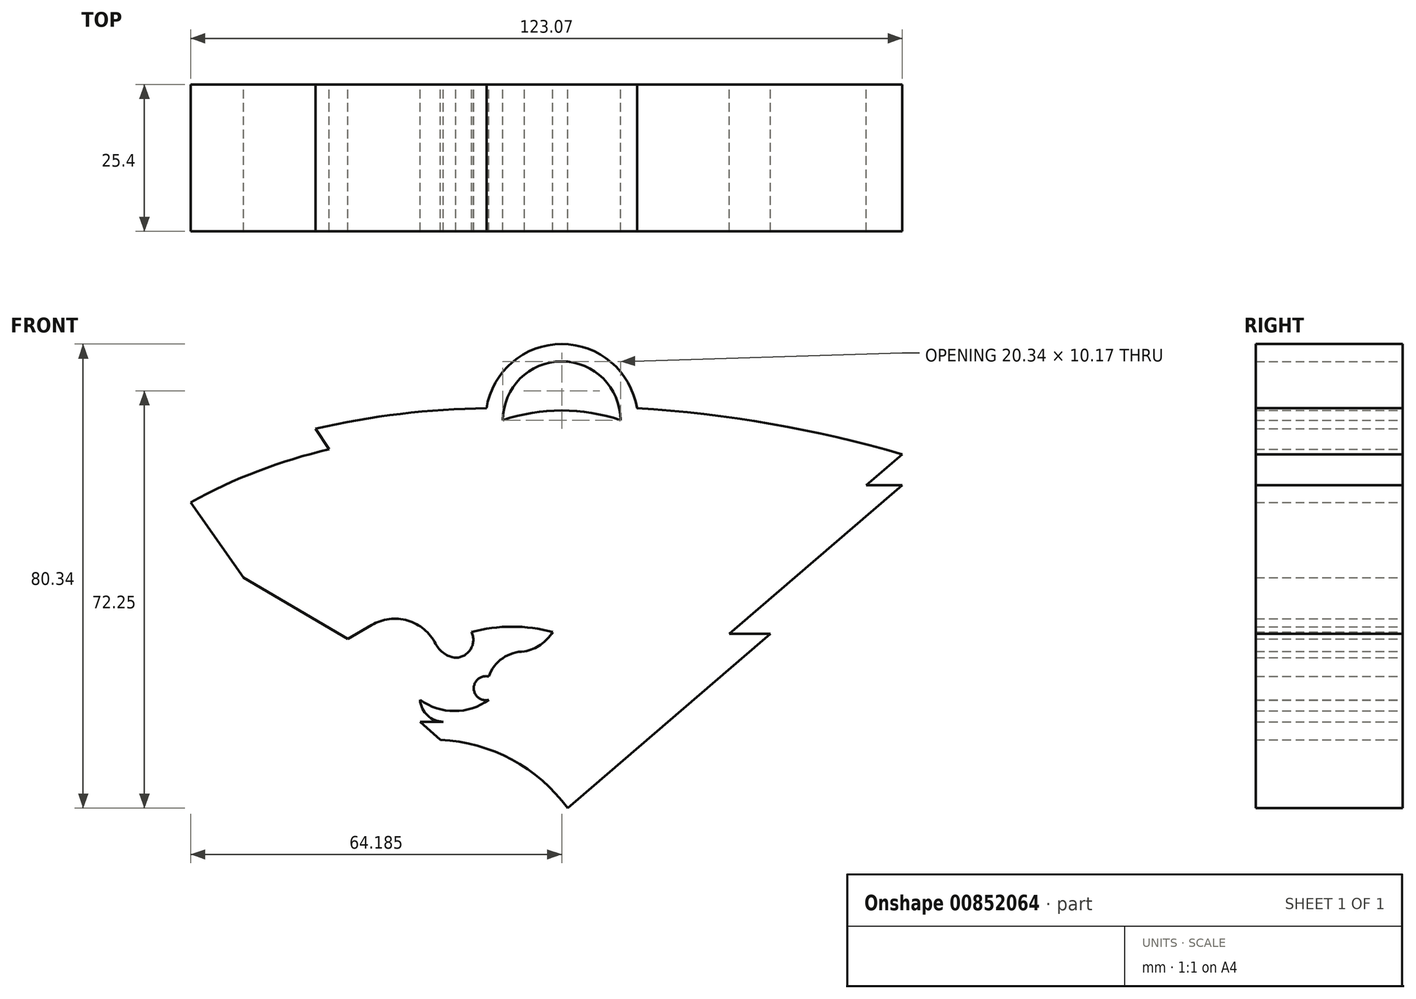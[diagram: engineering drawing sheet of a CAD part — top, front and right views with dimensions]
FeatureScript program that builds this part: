
annotation { "Feature Type Name" : "Feature", "Feature Type Description" : "" }
export const myFeature = defineFeature(function(context is Context, id is Id, definition is map)
    precondition{}
    {
        {
            var Q0;
            Q0=qCreatedBy(makeId("Front.planeOp"),FACE);
            var sketch = newSketch(context, id + "F0", { "sketchPlane" : qUnion([Q0])});
            skLineSegment(sketch, "E0", {"start": v(0, -55.9) * mm, "end": v(35.05, -25.73) * mm});
            skLineSegment(sketch, "E1", {"start": v(35.05, -25.73) * mm, "end": v(27.95, -25.73) * mm});
            skLineSegment(sketch, "E2", {"start": v(27.95, -25.73) * mm, "end": v(57.85, 0) * mm});
            skLineSegment(sketch, "E3", {"start": v(57.85, 0) * mm, "end": v(51.61, 0) * mm});
            skLineSegment(sketch, "E4", {"start": v(51.61, 0) * mm, "end": v(57.85, 5.37) * mm});
            skArc(sketch, "E5", {"start": v(57.85, 5.37) * mm, "mid": v(35.14, 10.63) * mm, "end": v(11.98, 13.31) * mm});
            skArc(sketch, "E6", {"start": v(11.98, 13.31) * mm, "mid": v(-1.04, 24.44) * mm, "end": v(-14.05, 13.31) * mm});
            skArc(sketch, "E7", {"start": v(-14.05, 13.31) * mm, "mid": v(-28.94, 12.34) * mm, "end": v(-43.63, 9.76) * mm});
            skLineSegment(sketch, "E8", {"start": v(-43.63, 9.76) * mm, "end": v(-41.26, 6.21) * mm});
            skArc(sketch, "E9", {"start": v(-41.26, 6.21) * mm, "mid": v(-53.56, 2.45) * mm, "end": v(-65.22, -2.96) * mm});
            skLineSegment(sketch, "E10", {"start": v(-65.22, -2.96) * mm, "end": v(-56.05, -15.97) * mm});
            skLineSegment(sketch, "E11", {"start": v(-56.05, -15.97) * mm, "end": v(-38, -26.62) * mm});
            skArc(sketch, "E12", {"start": v(0, -55.9) * mm, "mid": v(-9.67, -47.48) * mm, "end": v(-22.04, -44.07) * mm});
            skLineSegment(sketch, "E13", {"start": v(-38, -26.62) * mm, "end": v(-33.9, -24.2) * mm});
            skArc(sketch, "E14", {"start": v(-22.83, -27.44) * mm, "mid": v(-27.67, -23.43) * mm, "end": v(-33.9, -24.2) * mm});
            skArc(sketch, "E15", {"start": v(-22.83, -27.44) * mm, "mid": v(-21.39, -29.1) * mm, "end": v(-19.33, -29.87) * mm});
            skLineSegment(sketch, "E16", {"start": v(-22.04, -44.07) * mm, "end": v(-25.53, -40.93) * mm});
            skLineSegment(sketch, "E17", {"start": v(-25.53, -40.93) * mm, "end": v(-21.48, -40.93) * mm});
            skArc(sketch, "E18", {"start": v(-25.53, -37.15) * mm, "mid": v(-24.25, -39.84) * mm, "end": v(-21.48, -40.93) * mm});
            skArc(sketch, "E19", {"start": v(-25.53, -37.15) * mm, "mid": v(-19.6, -39.08) * mm, "end": v(-13.66, -37.15) * mm});
            skArc(sketch, "E20", {"start": v(-13.66, -33.1) * mm, "mid": v(-16.24, -35.13) * mm, "end": v(-13.66, -37.15) * mm});
            skArc(sketch, "E21", {"start": v(-7.46, -28.8) * mm, "mid": v(-11.26, -29.95) * mm, "end": v(-13.66, -33.1) * mm});
            skArc(sketch, "E22", {"start": v(-19.33, -29.87) * mm, "mid": v(-16.78, -28.36) * mm, "end": v(-16.63, -25.4) * mm});
            skArc(sketch, "E23", {"start": v(-2.6, -25.4) * mm, "mid": v(-9.61, -24.48) * mm, "end": v(-16.63, -25.4) * mm});
            skArc(sketch, "E24", {"start": v(-7.46, -28.8) * mm, "mid": v(-4.68, -27.6) * mm, "end": v(-2.6, -25.4) * mm});
            skLineSegment(sketch, "E25", {"start": v(48.12, 2.78) * mm, "end": v(40.84, -4.5) * mm});
            skLineSegment(sketch, "E26", {"start": v(40.84, -4.5) * mm, "end": v(48.12, 2.78) * mm});
            skPoint(sketch, "E27.endSnap0", {"position": v(35.14, 10.63) * mm});
            skArc(sketch, "E28", {"start": v(9.13, 11.27) * mm, "mid": v(-1.04, 21.43) * mm, "end": v(-11.2, 11.27) * mm});
            skArc(sketch, "E29", {"start": v(48.12, 2.78) * mm, "mid": v(24.28, 7.55) * mm, "end": v(0, 8.71) * mm});
            skArc(sketch, "E30", {"start": v(9.13, 11.27) * mm, "mid": v(-1.04, 12.94) * mm, "end": v(-11.2, 11.27) * mm});
            skSolve(sketch);
        }
        {
            var Q0;
            Q0 = qSketchRegion(id + "F0", true);
            extrude(context, id + "F1", {"entities" : qUnion([Q0]), "depth" : 25.4 * mm, "offsetDistance" : 25.4 * mm});
        }
    });
